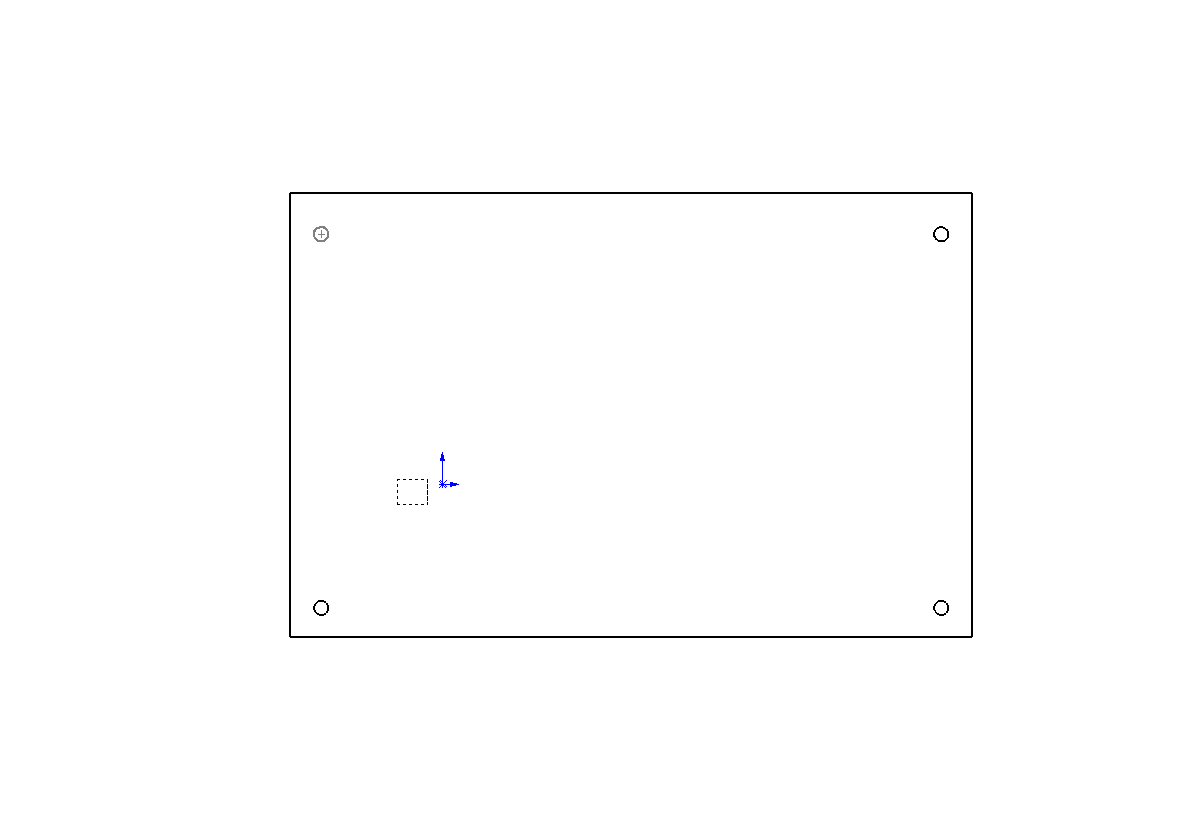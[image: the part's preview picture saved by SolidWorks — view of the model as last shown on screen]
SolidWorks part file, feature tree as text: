
SOLIDWORKS PART (.sldprt)
format: sldprt  version: not decoded by parser v0  size: 107,008 bytes
history: native  units: mm
features: sketch x3, extrude x2, material x1, cut_extrude x1, pattern_linear x1 (+13 scaffold rows collapsed)
feature tree (21):
  scaffold x13  (default folders/planes/origin — collapsed)
  material  "Material <not specified>"
  sketch  "Sketch1"  dims[D1=167.64mm D2=109.22mm]
  extrude  "PCB"  Depth=1.5748mm
  sketch  "Sketch2"  dims[D1=3.5mm D2=7.62mm D3=10.16mm]
  cut_extrude  "mount hole cut"  Depth=1.5748mm
  pattern_linear  "LPattern1"  Count1=2 Count2=2 Spacing1=152.5mm Spacing2=91.9mm
  sketch  "Sketch3"  dims[D1=22.5mm D2=63.43mm]
  extrude  "Extrude1"  Depth=3.75mm
decode coverage: 7 of 7 modeling features carry decoded parameters
note: suppression state not decoded; provenance and decode notes live in map.json
